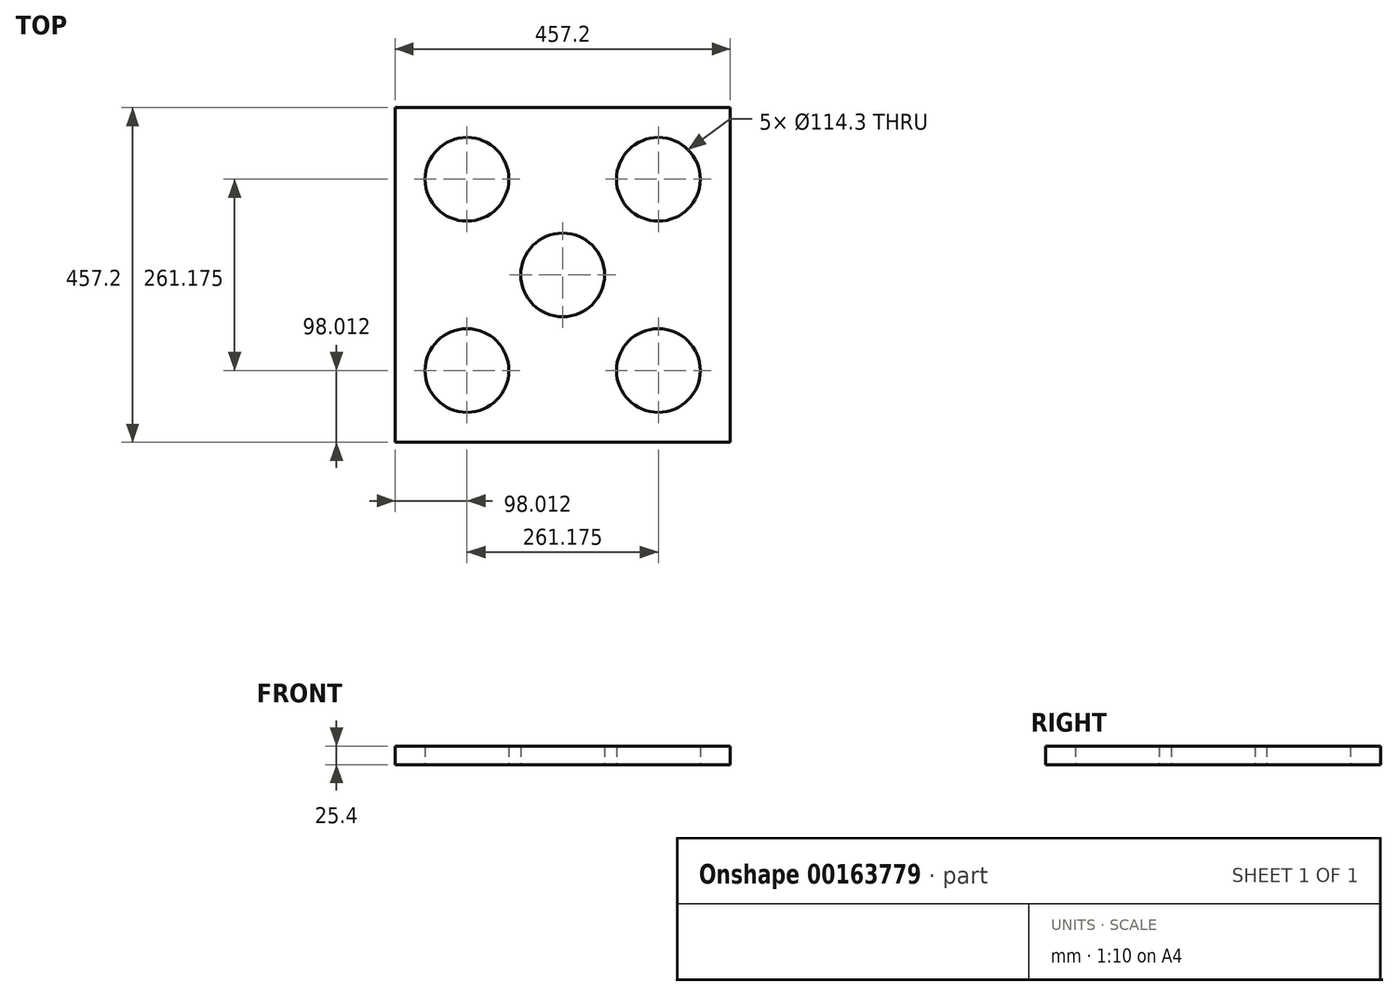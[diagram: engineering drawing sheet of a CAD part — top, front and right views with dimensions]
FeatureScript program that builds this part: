
annotation { "Feature Type Name" : "Feature", "Feature Type Description" : "" }
export const myFeature = defineFeature(function(context is Context, id is Id, definition is map)
    precondition{}
    {
        {
            var Q0;
            Q0=qCreatedBy(makeId("Top.planeOp"),FACE);
            var sketch = newSketch(context, id + "F0", { "sketchPlane" : qUnion([Q0])});
            skLineSegment(sketch, "E0.bottom", {"start": v(228.6, 228.6) * mm, "end": v(-228.6, 228.6) * mm});
            skLineSegment(sketch, "E0.top", {"start": v(228.6, -228.6) * mm, "end": v(-228.6, -228.6) * mm});
            skLineSegment(sketch, "E0.left", {"start": v(228.6, 228.6) * mm, "end": v(228.6, -228.6) * mm});
            skLineSegment(sketch, "E0.right", {"start": v(-228.6, 228.6) * mm, "end": v(-228.6, -228.6) * mm});
            skPoint(sketch, "E0.middle", {"position": v(0, 0) * mm});
            skCircle(sketch, "E1", {"center": v(0, 0) * mm, "radius": 57.15 * mm});
            skCircle(sketch, "E2", {"center": v(-130.59, -130.59) * mm, "radius": 57.15 * mm});
            skCircle(sketch, "E3", {"center": v(-130.59, 130.59) * mm, "radius": 57.15 * mm});
            skCircle(sketch, "E4", {"center": v(130.59, 130.59) * mm, "radius": 57.15 * mm});
            skCircle(sketch, "E5", {"center": v(130.59, -130.59) * mm, "radius": 57.15 * mm});
            skSolve(sketch);
        }
        {
            var Q0;
            Q0=makeQuery(id+"F0.imprint","IMPRINT",FACE,{"disambiguationData":[TD([[makeQuery(id+"F0.imprint","IMPRINT",EDGE,{"derivedFrom":sQuery(id+"F0.wireOp",EDGE,"E0.bottom")}),1.0]])]});
            extrude(context, id + "F1", {"entities" : qUnion([Q0]), "depth" : 25.4 * mm});
        }
    });
